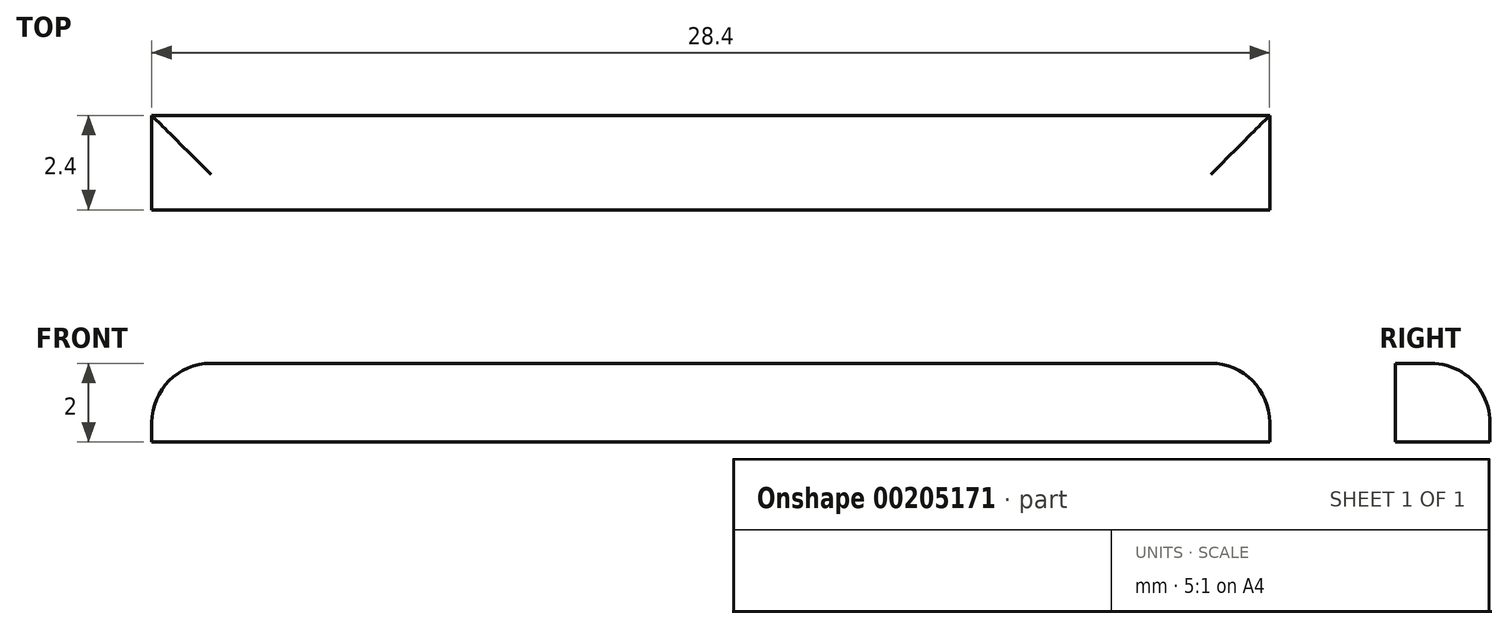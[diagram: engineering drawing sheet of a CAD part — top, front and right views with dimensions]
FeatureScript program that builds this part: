
annotation { "Feature Type Name" : "Feature", "Feature Type Description" : "" }
export const myFeature = defineFeature(function(context is Context, id is Id, definition is map)
    precondition{}
    {
        {
            var Q0;
            Q0=qCreatedBy(makeId("Top.planeOp"),FACE);
            var sketch = newSketch(context, id + "F0", { "sketchPlane" : qUnion([Q0])});
            skLineSegment(sketch, "E0.bottom", {"start": v(-53.58, 54.42) * mm, "end": v(-25.18, 54.42) * mm});
            skLineSegment(sketch, "E0.top", {"start": v(-53.58, 52.02) * mm, "end": v(-25.18, 52.02) * mm});
            skLineSegment(sketch, "E0.left", {"start": v(-53.58, 54.42) * mm, "end": v(-53.58, 52.02) * mm});
            skLineSegment(sketch, "E0.right", {"start": v(-25.18, 54.42) * mm, "end": v(-25.18, 52.02) * mm});
            skSolve(sketch);
        }
        {
            var Q0;
            Q0 = qSketchRegion(id + "F0", true);
            extrude(context, id + "F1", {"entities" : qUnion([Q0]), "depth" : 2 * mm});
        }
        {
            var Q0;
            Q0=makeQuery(id+"F1.opExtrude","CAP_EDGE",EDGE,{"disambiguationData":[OSD([sQuery(id+"F0.wireOp",EDGE,"E0.bottom")])],"isStart":false});
            var Q1;
            Q1=makeQuery(id+"F1.opExtrude","CAP_EDGE",EDGE,{"disambiguationData":[OSD([sQuery(id+"F0.wireOp",EDGE,"E0.right")])],"isStart":false});
            var Q2;
            Q2=makeQuery(id+"F1.opExtrude","CAP_EDGE",EDGE,{"disambiguationData":[OSD([sQuery(id+"F0.wireOp",EDGE,"E0.left")])],"isStart":false});
            fillet(context, id + "F2", {"entities" : qUnion([Q0, Q1, Q2]), "radius" : 1.5 * mm, "tangentPropagation" : true, "allowEdgeOverflow" : false});
        }
    });
